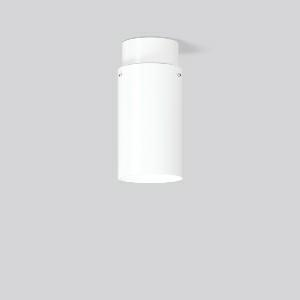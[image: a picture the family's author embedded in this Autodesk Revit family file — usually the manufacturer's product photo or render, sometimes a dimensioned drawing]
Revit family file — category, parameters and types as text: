
# Revit family: glasdownlight_931178_002_1_b1f8
name_source: partatom
category: Lighting Fixtures
units: mm (PartAtom-declared; Revit-internal decimal feet)

## family parameters
Cut with Voids When Loaded = No
Host = Face
Light Source = No
Part Type = Normal
Room Calculation Point = No
Round Connector Dimension = Use Diameter
Shared = No

## types (1)
- GLASDOWNLIGHT (1 x LED Modul 840, 2600 lm, 4000)
    Apparent Load = 21 VA
    CIE Flux Codes = 28 54 78 60 100
    Color Rendering = 80
    Color Temperature = 4000
    Default Elevation = 1800 mm
    Description = Series: GLASDOWNLIGHT
Decorative round surface-mounted luminaire. Base: aluminium, powder-coated. Mouth blown 3-layer opal glass (Triplex glass) with satin finish. Glass fastening: retaining screws. Triplex glass produces particularly homogeneous, soft and glare free lighting. 
Colour: white
Diameter: 150 mm
Height: 300 mm
Lamp: LED
Socket: without socket
Colour temperature: 4000K
Colour rendering index (CRI): 80
System power: 21 W
Rated luminous flux: 2600 lm
Luminous efficiency: 124 lm/W
Control gear: Regulated power supply
Protection class: I
Type of protection: IP 20
    Height = 300 mm
    Lamp = 1 x LED Modul 840
    Lamp Light Flux = 2600 lm
    Lamp count = 1
    Length = 150 mm
    Lifetime = 50000 h
    Luminous efficacy = 124 lm/W
    Manufacturer = RZB
    ModVariant = No
    Model = 931178.002.1
    Mounting Place = Ceiling
    Mounting Type = Surface mounted
    Number of Poles = 1
    OnlyDefault = Yes
    Power Factor = 1
    Product Name = GLASDOWNLIGHT
    Product group = Surface mounted ceiling luminaires
    ProductGroupID = 303
    Protection Class = Protection class I
    Protection Degree = IP 20
    RLX_Detail_Level = 1
    RLX_Emergency_Light_Flux = 0 lm
    RLX_Emergency_Type = 0
    RLX_Emergency_Type_DB = No
    RlxData = <blob elided: 14209 chars, md5=9260005c>
    Socket = socket
    Standby Power = 0 W
    System Light Flux = 2600 lm
    System Power = 21 W
    Type Comments = Product without accessories
    Type Image = 931178.002.jpg
    URL = http://relux.com
    VarID = ---
    Voltage = 230 V
    Voltage Range = 220-240 V
    Weight = 0.00 kg
    Width = 0 mm  [stored 0 ft]

note: [stored X ft] marks values corroborated as IEEE doubles in the binary element streams (Revit-internal decimal feet)

## geometry (parser evidence)
native form markers: Sweep x14
no freeform markers — native parametric forms only
